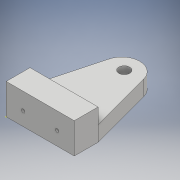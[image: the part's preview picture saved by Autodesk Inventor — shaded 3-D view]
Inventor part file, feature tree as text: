
AUTODESK INVENTOR PART (.ipt)
format: ipt  version: 2019 (Build 230136000, 136)  size: 127,488 bytes
history: native  units: mm
features: sketch x5, extrude x3
ambient origin geometry x8: Origin, YZ Plane, XZ Plane, XY Plane, X Axis, Y Axis, Z Axis, Center Point
bodies: Solid1 (feature_tree)
feature tree (8):
  sketch  "Sketch1"  dims[d9=4.5mm d10=0.0mm d11=4.5mm d12=0.0mm]
  sketch  "Sketch2"  dims[d13=1.0mm d14=1.0mm]
  sketch  "Sketch3"  dims[d15=5.5mm d16=0.0mm d17=7.0mm]
  extrude  "Extrusion1"  Depth=4.5mm TaperAngle=0.0deg
  extrude  "Extrusion2"  Depth=1.0mm
  extrude  "Extrusion3"  Depth=7.0mm
  sketch  "Sketch4"  dims[d18=6.999813mm]
  sketch  "Sketch5"  dims[d19=24.7mm d23=90.0deg d24=90.0deg d25=10.0mm d26=19.0mm d27=75.0deg d28=19.0mm d29=105.0deg d30=10.0mm d33=5.0mm d34=5.0mm]
